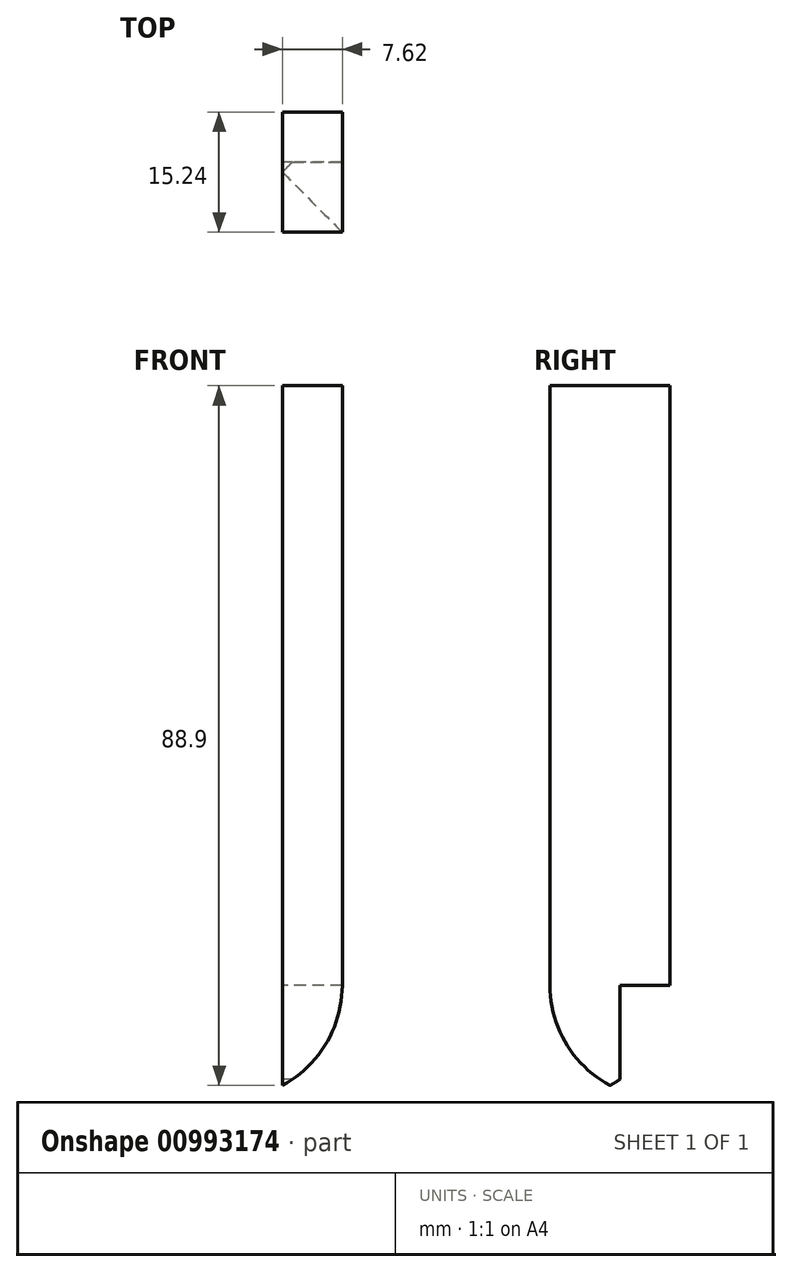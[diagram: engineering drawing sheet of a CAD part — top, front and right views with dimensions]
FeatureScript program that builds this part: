
annotation { "Feature Type Name" : "Feature", "Feature Type Description" : "" }
export const myFeature = defineFeature(function(context is Context, id is Id, definition is map)
    precondition{}
    {
        {
            var Q0;
            Q0=qCreatedBy(makeId("Right.planeOp"),FACE);
            var sketch = newSketch(context, id + "F0", { "sketchPlane" : qUnion([Q0])});
            skLineSegment(sketch, "E0.bottom", {"start": v(-48.78, 60.96) * mm, "end": v(-33.54, 60.96) * mm});
            skLineSegment(sketch, "E0.top", {"start": v(-48.78, -15.24) * mm, "end": v(-33.54, -15.24) * mm});
            skLineSegment(sketch, "E0.left", {"start": v(-48.78, 60.96) * mm, "end": v(-48.78, -15.24) * mm});
            skLineSegment(sketch, "E0.right", {"start": v(-33.54, 60.96) * mm, "end": v(-33.54, -15.24) * mm});
            skArc(sketch, "E1", {"start": v(-48.78, -15.24) * mm, "mid": v(-46.73, -22.65) * mm, "end": v(-41.16, -27.94) * mm});
            skPoint(sketch, "E1.endSnap0", {"position": v(-41.16, -15.24) * mm});
            skArc(sketch, "E2", {"start": v(-41.16, -27.94) * mm, "mid": v(-35.6, -22.65) * mm, "end": v(-33.54, -15.24) * mm});
            skLineSegment(sketch, "E3.bottom", {"start": v(-48.78, -15.24) * mm, "end": v(-42.43, -15.24) * mm});
            skLineSegment(sketch, "E4.bottom", {"start": v(-39.9, -27.94) * mm, "end": v(-33.54, -27.94) * mm});
            skLineSegment(sketch, "E4.top", {"start": v(-39.9, -15.24) * mm, "end": v(-33.54, -15.24) * mm});
            skLineSegment(sketch, "E4.left", {"start": v(-39.9, -27.94) * mm, "end": v(-39.9, -15.24) * mm});
            skLineSegment(sketch, "E4.right", {"start": v(-33.54, -27.94) * mm, "end": v(-33.54, -15.24) * mm});
            skSolve(sketch);
        }
        {
            var Q0;
            Q0=makeQuery(id+"F0.imprint","IMPRINT",FACE,{"disambiguationData":[TD([[makeQuery(id+"F0.imprint","IMPRINT",EDGE,{"derivedFrom":sQuery(id+"F0.wireOp",EDGE,"E0.bottom")}),-1.0]])]});
            var Q1;
            Q1=makeQuery(id+"F0.imprint","IMPRINT",FACE,{"disambiguationData":[TD([[makeQuery(id+"F0.imprint","IMPRINT",EDGE,{"derivedFrom":sQuery(id+"F0.wireOp",EDGE,"E0.top")}),-1.0]])]});
            extrude(context, id + "F1", {"entities" : qUnion([Q0, Q1]), "depth" : 7.62 * mm, "offsetDistance" : 25.4 * mm});
        }
        {
            var Q0;
            Q0=makeQuery(id+"F1.opExtrude","SWEPT_FACE",FACE,{"disambiguationData":[OSD([sQuery(id+"F0.wireOp",EDGE,"E0.right")])]});
            var sketch = newSketch(context, id + "F2", { "sketchPlane" : qUnion([Q0])});
            skLineSegment(sketch, "E5.bottom", {"start": v(0, -15.24) * mm, "end": v(-7.62, -15.24) * mm});
            skLineSegment(sketch, "E5.top", {"start": v(0, -27.94) * mm, "end": v(-7.62, -27.94) * mm});
            skLineSegment(sketch, "E5.left", {"start": v(0, -15.24) * mm, "end": v(0, -27.94) * mm});
            skLineSegment(sketch, "E5.right", {"start": v(-7.62, -15.24) * mm, "end": v(-7.62, -27.94) * mm});
            skArc(sketch, "E6", {"start": v(-7.62, -15.24) * mm, "mid": v(-5.57, -22.65) * mm, "end": v(0, -27.94) * mm});
            skSolve(sketch);
        }
        {
            var Q0;
            Q0=makeQuery(id+"F2.imprint","IMPRINT",FACE,{"disambiguationData":[TD([[makeQuery(id+"F2.imprint","IMPRINT",EDGE,{"derivedFrom":sQuery(id+"F2.wireOp",EDGE,"E5.top")}),-1.0]])]});
            extrude(context, id + "F3", {"entities" : qUnion([Q0]), "operationType" : NewBodyOperationType.REMOVE, "oppositeDirection" : true, "depth" : 25.4 * mm, "offsetDistance" : 25.4 * mm});
        }
    });
